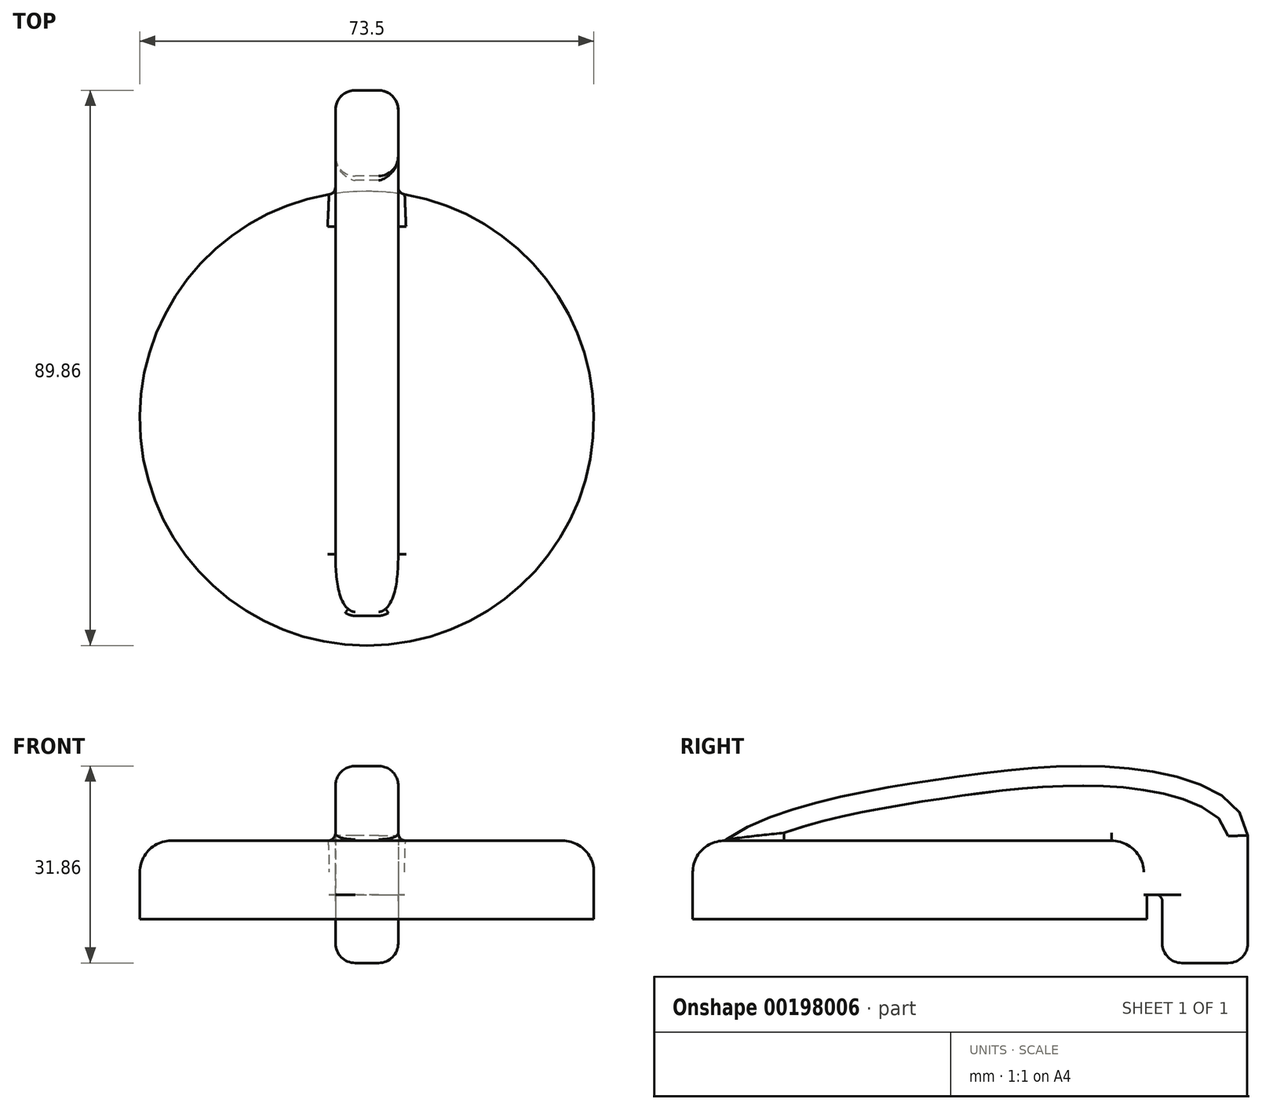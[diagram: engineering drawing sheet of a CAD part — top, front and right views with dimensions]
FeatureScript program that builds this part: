
annotation { "Feature Type Name" : "Feature", "Feature Type Description" : "" }
export const myFeature = defineFeature(function(context is Context, id is Id, definition is map)
    precondition{}
    {
        {
            var Q0;
            Q0=qCreatedBy(makeId("Top.planeOp"),FACE);
            var sketch = newSketch(context, id + "F0", { "sketchPlane" : qUnion([Q0])});
            skCircle(sketch, "E0", {"center": v(0, 0) * mm, "radius": 36.75 * mm});
            skSolve(sketch);
        }
        {
            var Q0;
            Q0 = qSketchRegion(id + "F0", true);
            extrude(context, id + "F1", {"entities" : qUnion([Q0]), "depth" : 12.7 * mm});
        }
        {
            var Q0;
            Q0=qCreatedBy(makeId("Right.planeOp"),FACE);
            var sketch = newSketch(context, id + "F2", { "sketchPlane" : qUnion([Q0])});
            skLineSegment(sketch, "E1", {"start": v(39.24, 2.92) * mm, "end": v(39.24, -3.9) * mm});
            skFitSpline(sketch, "E2", {"points": [v(-36.75, 5.43) * mm, v(0, 22.2) * mm, v(39.59, 23.52) * mm, v(53.1, 13.57) * mm], "startDerivative": vector(15.35, 81.77) * mm, "endDerivative": vector(4.43, -66.5) * mm});
            skLineSegment(sketch, "E3", {"start": v(53.1, 13.57) * mm, "end": v(53.1, -3.9) * mm});
            skLineSegment(sketch, "E4", {"start": v(42.42, -7.07) * mm, "end": v(49.93, -7.07) * mm});
            skPoint(sketch, "E5.visualSharp", {"position": v(39.24, -7.07) * mm});
            skArc(sketch, "E5.filletArc", {"start": v(39.24, -3.9) * mm, "mid": v(40.17, -6.14) * mm, "end": v(42.42, -7.07) * mm});
            skPoint(sketch, "E6.visualSharp", {"position": v(53.1, -7.07) * mm});
            skArc(sketch, "E6.filletArc", {"start": v(49.93, -7.07) * mm, "mid": v(52.18, -6.14) * mm, "end": v(53.1, -3.9) * mm});
            skPoint(sketch, "E7.visualSharp", {"position": v(39.24, 3.93) * mm});
            skArc(sketch, "E7.filletArc", {"start": v(39.24, 2.92) * mm, "mid": v(39.05, 3.54) * mm, "end": v(38.54, 3.93) * mm});
            skLineSegment(sketch, "E8", {"start": v(38.54, 3.93) * mm, "end": v(29.45, 3.93) * mm});
            skLineSegment(sketch, "E9", {"start": v(29.45, 3.93) * mm, "end": v(29.45, 12.7) * mm});
            skPoint(sketch, "E10.orphan", {"position": v(36.75, 12.7) * mm});
            skLineSegment(sketch, "E11", {"start": v(29.45, 12.7) * mm, "end": v(-31.6, 12.7) * mm});
            skSolve(sketch);
        }
        {
            var Q0;
            Q0 = qSketchRegion(id + "F2", true);
            extrude(context, id + "F3", {"entities" : qUnion([Q0]), "operationType" : NewBodyOperationType.ADD, "depth" : 5.08 * mm, "hasSecondDirection" : true, "secondDirectionOppositeDirection" : true, "secondDirectionDepth" : 5.08 * mm});
        }
        {
            var Q0;
            Q0=makeQuery(id+"F3.opExtrude","CAP_EDGE",EDGE,{"disambiguationData":[OSD([sQuery(id+"F2.wireOp",EDGE,"E2")])],"isStart":false});
            var Q1;
            Q1=makeQuery(id+"F3.opExtrude","CAP_EDGE",EDGE,{"disambiguationData":[OSD([sQuery(id+"F2.wireOp",EDGE,"E2")])],"isStart":true});
            var Q2;
            Q2=makeQuery(id+"F3.opExtrude","CAP_EDGE",EDGE,{"disambiguationData":[OSD([sQuery(id+"F2.wireOp",EDGE,"E6.filletArc")])],"isStart":false});
            var Q3;
            Q3=makeQuery(id+"F3.opExtrude","CAP_EDGE",EDGE,{"disambiguationData":[OSD([sQuery(id+"F2.wireOp",EDGE,"E6.filletArc")])],"isStart":true});
            fillet(context, id + "F4", {"entities" : qUnion([Q0, Q1, Q2, Q3]), "radius" : 3.17 * mm, "tangentPropagation" : true, "allowEdgeOverflow" : false});
        }
        {
            var Q0;
            Q0=makeQuery(id+"F1.opExtrude","CAP_EDGE",EDGE,{"disambiguationData":[OSD([sQuery(id+"F0.wireOp",EDGE,"E0")])],"isStart":false});
            fillet(context, id + "F5", {"entities" : qUnion([Q0]), "radius" : 5.08 * mm, "tangentPropagation" : true, "allowEdgeOverflow" : false});
        }
        {
            var Q0;
            Q0=makeQuery(id+"F3.boolean.opBoolean","INTERSECT",EDGE,{"derivedFrom":[makeQuery(id+"F1.opExtrude","CAP_FACE",FACE,{"disambiguationData":[OSD([sQuery(id+"F0.wireOp",EDGE,"E0")])],"isStart":false}),makeQuery(id+"F3.opExtrude","CAP_FACE",FACE,{"disambiguationData":[OSD([sQuery(id+"F2.wireOp",EDGE,"E1"),sQuery(id+"F2.wireOp",EDGE,"E2"),sQuery(id+"F2.wireOp",EDGE,"E3"),sQuery(id+"F2.wireOp",EDGE,"E4"),sQuery(id+"F2.wireOp",EDGE,"E5.filletArc"),sQuery(id+"F2.wireOp",EDGE,"E6.filletArc"),sQuery(id+"F2.wireOp",EDGE,"E7.filletArc"),sQuery(id+"F2.wireOp",EDGE,"E8"),sQuery(id+"F2.wireOp",EDGE,"E9"),sQuery(id+"F2.wireOp",EDGE,"E11")])],"isStart":false})]});
            fillet(context, id + "F6", {"entities" : qUnion([Q0]), "radius" : 1.27 * mm, "tangentPropagation" : true, "allowEdgeOverflow" : false});
        }
    });
